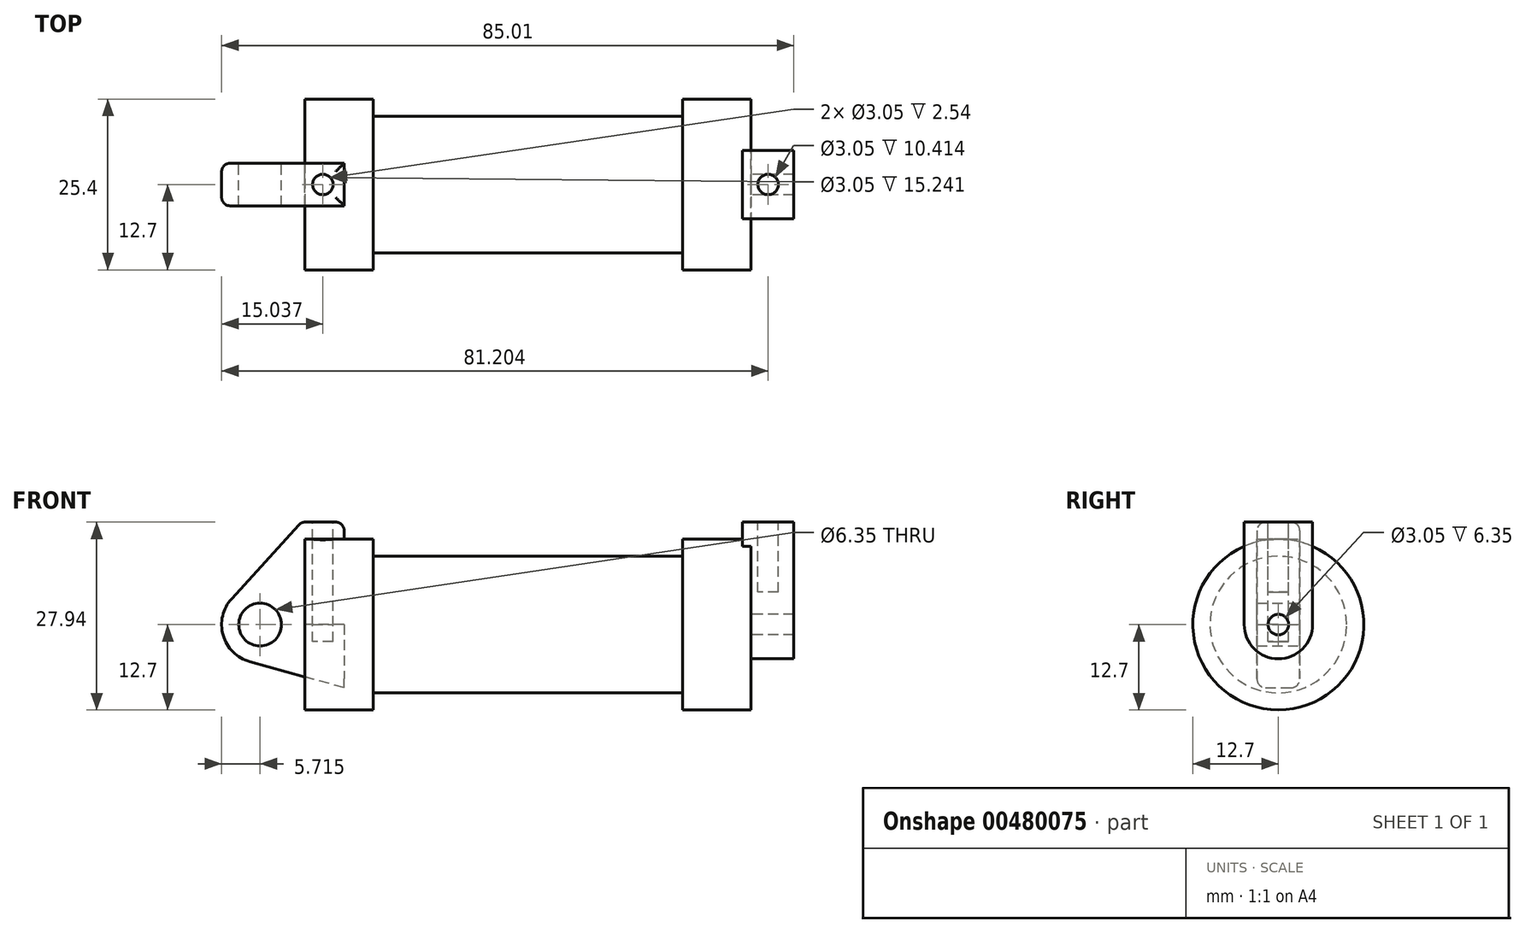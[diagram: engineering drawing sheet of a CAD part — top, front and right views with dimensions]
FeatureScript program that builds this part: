
annotation { "Feature Type Name" : "Feature", "Feature Type Description" : "" }
export const myFeature = defineFeature(function(context is Context, id is Id, definition is map)
    precondition{}
    {
        {
            var Q0;
            Q0=qCreatedBy(makeId("Front.planeOp"),FACE);
            var sketch = newSketch(context, id + "F0", { "sketchPlane" : qUnion([Q0])});
            skLineSegment(sketch, "E0", {"start": v(0, 0) * mm, "end": v(0, 12.7) * mm});
            skLineSegment(sketch, "E1", {"start": v(0, 12.7) * mm, "end": v(10.16, 12.7) * mm});
            skLineSegment(sketch, "E2", {"start": v(10.16, 12.7) * mm, "end": v(10.16, 10.16) * mm});
            skLineSegment(sketch, "E3", {"start": v(10.16, 10.16) * mm, "end": v(56.13, 10.16) * mm});
            skLineSegment(sketch, "E4", {"start": v(56.13, 10.16) * mm, "end": v(56.13, 12.7) * mm});
            skLineSegment(sketch, "E5", {"start": v(56.13, 12.7) * mm, "end": v(66.3, 12.7) * mm});
            skLineSegment(sketch, "E6", {"start": v(66.3, 12.7) * mm, "end": v(66.3, 0) * mm});
            skLineSegment(sketch, "E7", {"start": v(66.3, 0) * mm, "end": v(0, 0) * mm});
            skLineSegment(sketch, "E8", {"start": v(5.84, 15.24) * mm, "end": v(-0.5, 15.24) * mm});
            skLineSegment(sketch, "E9", {"start": v(-0.5, 15.24) * mm, "end": v(-10.88, 3.85) * mm});
            skLineSegment(sketch, "E10", {"start": v(0, 0) * mm, "end": v(-6.65, 0) * mm});
            skCircle(sketch, "E11", {"center": v(-6.65, 0) * mm, "radius": 5.72 * mm});
            skCircle(sketch, "E12", {"center": v(-6.65, 0) * mm, "radius": 3.18 * mm});
            skLineSegment(sketch, "E13", {"start": v(5.84, 15.24) * mm, "end": v(5.84, -9.4) * mm});
            skLineSegment(sketch, "E14", {"start": v(5.84, -9.4) * mm, "end": v(-8.18, -5.5) * mm});
            skSolve(sketch);
        }
        {
            var Q0;
            {var subQ0=sQuery(id+"F0.wireOp",EDGE,"E2");Q0=makeQuery(id+"F0.imprint","IMPRINT",FACE,{"disambiguationData":[TD([[makeQuery(id+"F0.imprint","IMPRINT",EDGE,{"derivedFrom":subQ0}),-1.0]])]});}
            var Q1;
            {var subQ0=sQuery(id+"F0.wireOp",EDGE,"E0");Q1=makeQuery(id+"F0.imprint","IMPRINT",FACE,{"disambiguationData":[TD([[makeQuery(id+"F0.imprint","IMPRINT",EDGE,{"derivedFrom":subQ0}),-1.0]])]});}
            var Q2;
            Q2=sQuery(id+"F0.wireOp",EDGE,"E7");
            revolve(context, id + "F1", {"entities" : qUnion([Q0, Q1]), "axis" : qUnion([Q2]), "revolveType" : RevolveType.FULL});
        }
        {
            var Q0;
            {var subQ1=sQuery(id+"F0.wireOp",EDGE,"E0");Q0=makeQuery(id+"F0.imprint","IMPRINT",FACE,{"disambiguationData":[TD([[makeQuery(id+"F0.imprint","IMPRINT",EDGE,{"derivedFrom":subQ1}),1.0]])]});}
            var Q1;
            {var subQ0=sQuery(id+"F0.wireOp",EDGE,"E14");Q1=makeQuery(id+"F0.imprint","IMPRINT",FACE,{"disambiguationData":[TD([[makeQuery(id+"F0.imprint","IMPRINT",EDGE,{"derivedFrom":subQ0}),-1.0]])]});}
            var Q2;
            {var subQ5=sQuery(id+"F0.wireOp",EDGE,"E12");Q2=makeQuery(id+"F0.imprint","IMPRINT",FACE,{"disambiguationData":[TD([[makeQuery(id+"F0.imprint","IMPRINT",EDGE,{"derivedFrom":subQ5}),-1.0]])]});}
            extrude(context, id + "F2", {"entities" : qUnion([Q0, Q1, Q2]), "endBound" : BoundingType.SYMMETRIC, "depth" : 6.35 * mm});
        }
        {
            var Q0;
            Q0=makeQuery(id+"F1.opRevolve","SWEPT_FACE",FACE,{"disambiguationData":[OSD([sQuery(id+"F0.wireOp",EDGE,"E6")])]});
            var sketch = newSketch(context, id + "F3", { "sketchPlane" : qUnion([Q0])});
            skCircle(sketch, "E15", {"center": v(0, 0) * mm, "radius": 5.08 * mm});
            skCircle(sketch, "E16", {"center": v(0, 0) * mm, "radius": 1.52 * mm});
            skLineSegment(sketch, "E17", {"start": v(-5.08, 0) * mm, "end": v(-5.08, 15.24) * mm});
            skLineSegment(sketch, "E18", {"start": v(5.08, 0) * mm, "end": v(5.08, 15.24) * mm});
            skLineSegment(sketch, "E19", {"start": v(5.08, 15.24) * mm, "end": v(-5.08, 15.24) * mm});
            skSolve(sketch);
        }
        {
            var Q0;
            Q0=makeQuery(id+"F3.imprint","IMPRINT",FACE,{"disambiguationData":[TD([[makeQuery(id+"F3.imprint","IMPRINT",EDGE,{"derivedFrom":sQuery(id+"F3.wireOp",EDGE,"E16")}),-1.0]])]});
            var Q1;
            {var subQ0=sQuery(id+"F3.wireOp",EDGE,"E19");Q1=makeQuery(id+"F3.imprint","IMPRINT",FACE,{"disambiguationData":[TD([[makeQuery(id+"F3.imprint","IMPRINT",EDGE,{"derivedFrom":subQ0}),1.0]])]});}
            var Q2;
            {var subQ0=sQuery(id+"F3.wireOp",EDGE,"E17");var subQ1=sQuery(id+"F3.wireOp",EDGE,"E15");var subQ2=makeQuery(id+"F3.imprint","INTERSECT",VERTEX,{"derivedFrom":[subQ1,subQ0]});Q2=makeQuery(id+"F3.imprint","IMPRINT",FACE,{"disambiguationData":[TD([[makeQuery(id+"F3.imprint","IMPRINT",EDGE,{"disambiguationData":[TD([[subQ2,1.0]])],"derivedFrom":subQ1}),-1.0]])]});}
            extrude(context, id + "F4", {"entities" : qUnion([Q0, Q1, Q2]), "operationType" : NewBodyOperationType.ADD, "depth" : 6.35 * mm, "hasSecondDirection" : true, "secondDirectionOppositeDirection" : true, "secondDirectionDepth" : 1.27 * mm});
        }
        {
            var Q0;
            Q0=makeQuery(id+"F2.opExtrude","SWEPT_FACE",FACE,{"disambiguationData":[OSD([sQuery(id+"F0.wireOp",EDGE,"E8")])]});
            var sketch = newSketch(context, id + "F5", { "sketchPlane" : qUnion([Q0])});
            skCircle(sketch, "E20", {"center": v(2.67, 0) * mm, "radius": 1.52 * mm});
            skSolve(sketch);
        }
        {
            var Q0;
            Q0=makeQuery(id+"F4.opExtrude","SWEPT_FACE",FACE,{"disambiguationData":[OSD([sQuery(id+"F3.wireOp",EDGE,"E19")])]});
            var sketch = newSketch(context, id + "F6", { "sketchPlane" : qUnion([Q0])});
            skCircle(sketch, "E21", {"center": v(68.83, 0) * mm, "radius": 1.52 * mm});
            skPoint(sketch, "E21.centerSnap0", {"position": v(72.64, 0) * mm});
            skPoint(sketch, "E21.centerSnap1", {"position": v(68.83, 5.08) * mm});
            skSolve(sketch);
        }
        {
            var Q0;
            Q0=makeQuery(id+"F6.imprint","IMPRINT",FACE,{"disambiguationData":[TD([[makeQuery(id+"F6.imprint","IMPRINT",EDGE,{"derivedFrom":sQuery(id+"F6.wireOp",EDGE,"E21")}),1.0]])]});
            extrude(context, id + "F7", {"entities" : qUnion([Q0]), "operationType" : NewBodyOperationType.REMOVE, "oppositeDirection" : true, "depth" : 10.4 * mm});
        }
        {
            var Q0;
            Q0=makeQuery(id+"F5.imprint","IMPRINT",FACE,{"disambiguationData":[TD([[makeQuery(id+"F5.imprint","IMPRINT",EDGE,{"derivedFrom":sQuery(id+"F5.wireOp",EDGE,"E20")}),1.0]])]});
            extrude(context, id + "F8", {"entities" : qUnion([Q0]), "operationType" : NewBodyOperationType.REMOVE, "oppositeDirection" : true, "depth" : 17.78 * mm});
        }
        {
            var Q0;
            Q0=makeQuery(id+"F1.opRevolve","SWEPT_EDGE",EDGE,{"disambiguationData":[OSD([sQuery(id+"F0.wireOp",EDGE,"E1"),sQuery(id+"F0.wireOp",EDGE,"E2")])]});
            var Q1;
            Q1=makeQuery(id+"F1.opRevolve","SWEPT_EDGE",EDGE,{"disambiguationData":[OSD([sQuery(id+"F0.wireOp",EDGE,"E0"),sQuery(id+"F0.wireOp",EDGE,"E1")])]});
            var Q2;
            Q2=makeQuery(id+"F1.opRevolve","SWEPT_EDGE",EDGE,{"disambiguationData":[OSD([sQuery(id+"F0.wireOp",EDGE,"E4"),sQuery(id+"F0.wireOp",EDGE,"E5")])]});
            var Q3;
            Q3=makeQuery(id+"F1.opRevolve","SWEPT_EDGE",EDGE,{"disambiguationData":[OSD([sQuery(id+"F0.wireOp",EDGE,"E5"),sQuery(id+"F0.wireOp",EDGE,"E6")])]});
            var Q4;
            Q4=makeQuery(id+"F4.opExtrude","CAP_EDGE",EDGE,{"disambiguationData":[OSD([sQuery(id+"F3.wireOp",EDGE,"E19")])],"isStart":true});
            var Q5;
            Q5=makeQuery(id+"F4.opExtrude","SWEPT_EDGE",EDGE,{"disambiguationData":[OSD([sQuery(id+"F3.wireOp",EDGE,"E17"),sQuery(id+"F3.wireOp",EDGE,"E19")])]});
            var Q6;
            Q6=makeQuery(id+"F4.opExtrude","CAP_EDGE",EDGE,{"disambiguationData":[OSD([sQuery(id+"F3.wireOp",EDGE,"E19")])],"isStart":false});
            var Q7;
            Q7=makeQuery(id+"F4.opExtrude","SWEPT_EDGE",EDGE,{"disambiguationData":[OSD([sQuery(id+"F3.wireOp",EDGE,"E18"),sQuery(id+"F3.wireOp",EDGE,"E19")])]});
            var Q8;
            Q8=makeQuery(id+"F4.opExtrude","CAP_EDGE",EDGE,{"disambiguationData":[OSD([sQuery(id+"F3.wireOp",EDGE,"E17")])],"isStart":false});
            var Q9;
            Q9=makeQuery(id+"F4.opExtrude","CAP_EDGE",EDGE,{"disambiguationData":[OSD([sQuery(id+"F3.wireOp",EDGE,"E15")])],"isStart":false});
            var Q10;
            Q10=makeQuery(id+"F4.boolean.opBoolean","INTERSECT",EDGE,{"derivedFrom":[makeQuery(id+"F1.opRevolve","SWEPT_FACE",FACE,{"disambiguationData":[OSD([sQuery(id+"F0.wireOp",EDGE,"E6")])]}),makeQuery(id+"F4.opExtrude","SWEPT_FACE",FACE,{"disambiguationData":[OSD([sQuery(id+"F3.wireOp",EDGE,"E15")])]})]});
            var Q11;
            Q11=makeQuery(id+"F4.boolean.opBoolean","INTERSECT",EDGE,{"derivedFrom":[makeQuery(id+"F1.opRevolve","SWEPT_FACE",FACE,{"disambiguationData":[OSD([sQuery(id+"F0.wireOp",EDGE,"E6")])]}),makeQuery(id+"F4.opExtrude","SWEPT_FACE",FACE,{"disambiguationData":[OSD([sQuery(id+"F3.wireOp",EDGE,"E17")])]})]});
            var Q12;
            Q12=makeQuery(id+"F4.boolean.opBoolean","INTERSECT",EDGE,{"derivedFrom":[makeQuery(id+"F1.opRevolve","SWEPT_FACE",FACE,{"disambiguationData":[OSD([sQuery(id+"F0.wireOp",EDGE,"E6")])]}),makeQuery(id+"F4.opExtrude","SWEPT_FACE",FACE,{"disambiguationData":[OSD([sQuery(id+"F3.wireOp",EDGE,"E18")])]})]});
            var Q13;
            Q13=makeQuery(id+"F2.opExtrude","CAP_EDGE",EDGE,{"disambiguationData":[OSD([sQuery(id+"F0.wireOp",EDGE,"E9")])],"isStart":false});
            var Q14;
            Q14=makeQuery(id+"F2.opExtrude","CAP_EDGE",EDGE,{"disambiguationData":[OSD([sQuery(id+"F0.wireOp",EDGE,"E9")])],"isStart":true});
            var Q15;
            Q15=makeQuery(id+"F2.opExtrude","CAP_EDGE",EDGE,{"disambiguationData":[OSD([sQuery(id+"F0.wireOp",EDGE,"E11")])],"isStart":true});
            var Q16;
            Q16=makeQuery(id+"F2.opExtrude","CAP_EDGE",EDGE,{"disambiguationData":[OSD([sQuery(id+"F0.wireOp",EDGE,"E11")])],"isStart":false});
            var Q17;
            Q17=makeQuery(id+"F2.opExtrude","CAP_EDGE",EDGE,{"disambiguationData":[OSD([sQuery(id+"F0.wireOp",EDGE,"E14")])],"isStart":false});
            var Q18;
            Q18=makeQuery(id+"F2.opExtrude","CAP_EDGE",EDGE,{"disambiguationData":[OSD([sQuery(id+"F0.wireOp",EDGE,"E14")])],"isStart":true});
            var Q19;
            Q19=makeQuery(id+"F2.opExtrude","CAP_EDGE",EDGE,{"disambiguationData":[OSD([sQuery(id+"F0.wireOp",EDGE,"E8")])],"isStart":false});
            var Q20;
            Q20=makeQuery(id+"F2.opExtrude","SWEPT_EDGE",EDGE,{"disambiguationData":[OSD([sQuery(id+"F0.wireOp",EDGE,"E8"),sQuery(id+"F0.wireOp",EDGE,"E9")])]});
            var Q21;
            Q21=makeQuery(id+"F2.opExtrude","CAP_EDGE",EDGE,{"disambiguationData":[OSD([sQuery(id+"F0.wireOp",EDGE,"E8")])],"isStart":true});
            var Q22;
            Q22=makeQuery(id+"F2.opExtrude","SWEPT_EDGE",EDGE,{"disambiguationData":[OSD([sQuery(id+"F0.wireOp",EDGE,"E8"),sQuery(id+"F0.wireOp",EDGE,"E13")])]});
            var Q23;
            Q23=makeQuery(id+"F1.opRevolve","SWEPT_EDGE",EDGE,{"disambiguationData":[OSD([sQuery(id+"F0.wireOp",EDGE,"E2"),sQuery(id+"F0.wireOp",EDGE,"E3")])]});
            var Q24;
            Q24=makeQuery(id+"F1.opRevolve","SWEPT_EDGE",EDGE,{"disambiguationData":[OSD([sQuery(id+"F0.wireOp",EDGE,"E3"),sQuery(id+"F0.wireOp",EDGE,"E4")])]});
            fillet(context, id + "F9", {"entities" : qUnion([Q0, Q1, Q2, Q3, Q4, Q5, Q6, Q7, Q8, Q9, Q10, Q11, Q12, Q13, Q14, Q15, Q16, Q17, Q18, Q19, Q20, Q21, Q22, Q23, Q24]), "radius" : 1.27 * mm, "tangentPropagation" : true, "allowEdgeOverflow" : false});
        }
    });
